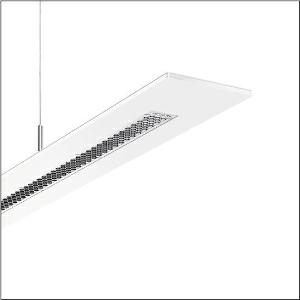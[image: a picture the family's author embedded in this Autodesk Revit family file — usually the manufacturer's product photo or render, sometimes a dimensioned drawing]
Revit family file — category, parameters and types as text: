
# Revit family: arktika_r__21_duo_5mb252dl60840_f6f7
name_source: partatom
category: Lighting Fixtures
units: mm (PartAtom-declared; Revit-internal decimal feet)

## family parameters
Cut with Voids When Loaded = No
Host = Face
Light Source = No
Part Type = Normal
Room Calculation Point = No
Round Connector Dimension = Use Diameter
Shared = No

## types (1)
- --- (1 x LED 4000K / CRI = 80 (unbekannt), 8800 lm, 4000K)
    Apparent Load = 67 VA
    CIE Flux Codes = 81 100 100 79 100
    Color Rendering = 80
    Color Temperature = 4000K
    Default Elevation = 1800 mm
    Description = Arktika® 21 duo, office luminaire, primary anti-glare with honeycomb louvre, of plastic, aluminium vaporised, highly specular, light emission: direct/indirect distribution, primary light characteristic: symmetric, installation type: suspended mounting, LED, rated luminous flux: 8.800lm, luminous efficacy: 132lm/W, light colour: 840, colour temperature: 4000K, control gear: ECG DALI, with terminal, 3+2-pole, max. 2.5mm², mains connection: 220..240V, AC, 50/60Hz, rated input power: 67W, housing, of aluminium, powder-coated, traffic white (RAL 9016), 2-length, length: 2.280mm, width: 120mm, height: 8mm, protection rating (complete): IP20, insulation class (complete): insulation class II (safety insulation), certification: CE, packaging unit: 1 piece
    Height = 8 mm  [stored 0.0262467 ft]
    Lamp = 1 x LED 4000K / CRI >= 80 (unbekannt)
    Lamp Light Flux = 8800 lm
    Lamp count = 1
    Length = 2280 mm
    Luminous efficacy = 132 lm/W
    Manufacturer = Siteco
    ModVariant = No
    Model = 5MB252DL60840
    Mounting Place = Ceiling
    Mounting Type = Pendant
    Number of Poles = 1
    OnlyDefault = Yes
    Power Factor = 1
    Product Name = Arktika® 21 duo
    Product group = office luminaire | ceiling pendant
    ProductGroupID = 902
    Protection Class = Protection class II
    Protection Degree = IP 20
    RLX_Detail_Level = 1
    RLX_Emergency_Light_Flux = 0 lm
    RLX_Emergency_Type = 0
    RLX_Emergency_Type_DB = No
    RlxData = <blob elided: 39733 chars, md5=adc02821>
    Socket = socket
    Standby Power = 0 W
    System Light Flux = 8800 lm
    System Power = 67 W
    Type Comments = factory setting: luminous flux: 100 % | dim-lin: 254 | 1330 mA
    Type Image = l_1006128.jpg
    URL = http://relux.com
    VarID = @adj_164477
    Voltage = 0 V
    Weight = 0.00 kg
    Width = 120 mm

note: [stored X ft] marks values corroborated as IEEE doubles in the binary element streams (Revit-internal decimal feet)

## geometry (parser evidence)
native form markers: Blend x4, Sweep x13
no freeform markers — native parametric forms only
